# Revit family: Shower-Valve_Trim-KOHLER-PURIST-K-15577A
name_source: partatom
category: Specialty Equipment
revit_build: Autodesk Revit 2017 (Build: 20160225_1515(x64)
units: mm (PartAtom-declared; Revit-internal decimal feet)

## family parameters
Cut with Voids When Loaded = No
Host = Face
OmniClass Number = 23.31.25.00
OmniClass Title = Toilet and Bath Specialties
Part Type = Normal
Room Calculation Point = No
Round Connector Dimension = Use Diameter
Shared = No

## types (5) — shared parameters
ADA Compliant = No
Assembly Code = C1030200
Date Modified = 10/06/2020
Default Elevation = 42"
Description = SHOWER/ BATH MIXER TRIM KIT WITH DIVERTER
Height = 6 15/16"
Length = 4"
Manufacturer = KOHLER Co.
Master Format 2014 = 10 28 00
Master Format 2014 Name = Toilet, Bath, and Laundry Accessories
Material = Brass Construction
Product Name = PURIST
URL = https://www.kohlerasiapacific.com
WaterSense Certified = No
Width = 6 15/16"

## per-type parameters (varying)
| type | Finish | Model | Type |
| CP- Polished Chrome | Kohler-Metal-CP-Polished_Chrome | K-15577A-4-CP | 1 |
| BN- Brushed Nickel | Kohler-Metal-BN-Vibrant_Brushed_Nickel | K-15577A-4-BN | 2 |
| BV- Brushed Bronze | Kohler-Metal-BV-Brushed_Bronze | K-15577A-4-BV | 3 |
| PGD- Modern Polished Gold | Kohler-Metal-PGD-Modern_Polished_Gold | K-15577A-4-PGD | 4 |
| RGD- Polished Rose Gold | Kohler-Metal-RGD-Polished_Rose_Gold | K-15577A-4-RGD | 5 |

## geometry (parser evidence)
native form markers: Sweep x5
no freeform markers — native parametric forms only
